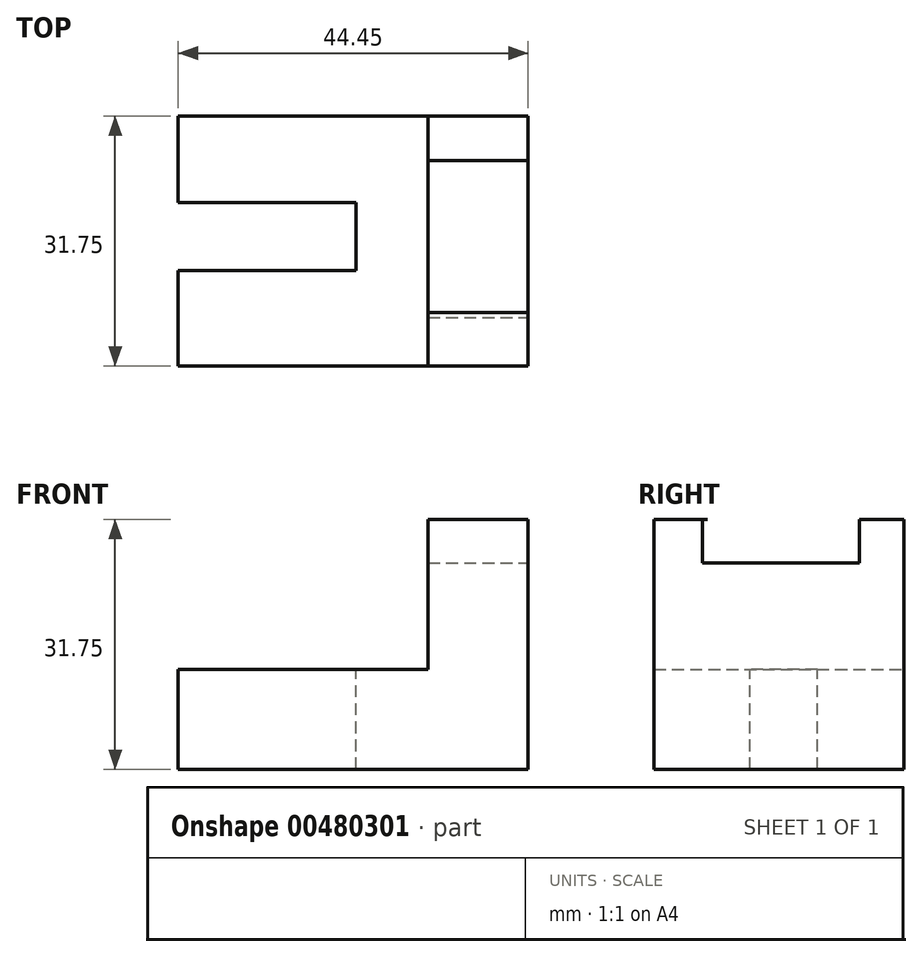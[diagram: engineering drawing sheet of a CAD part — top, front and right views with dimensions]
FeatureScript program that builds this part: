
annotation { "Feature Type Name" : "Feature", "Feature Type Description" : "" }
export const myFeature = defineFeature(function(context is Context, id is Id, definition is map)
    precondition{}
    {
        {
            var Q0;
            Q0=qCreatedBy(makeId("Front.planeOp"),FACE);
            var sketch = newSketch(context, id + "F0", { "sketchPlane" : qUnion([Q0])});
            skLineSegment(sketch, "E0", {"start": v(0, 0) * mm, "end": v(-44.45, 0) * mm});
            skLineSegment(sketch, "E1", {"start": v(-44.45, 0) * mm, "end": v(-44.45, 12.7) * mm});
            skLineSegment(sketch, "E2", {"start": v(-44.45, 12.7) * mm, "end": v(-12.7, 12.7) * mm});
            skLineSegment(sketch, "E3", {"start": v(-12.7, 12.7) * mm, "end": v(-12.7, 31.75) * mm});
            skLineSegment(sketch, "E4", {"start": v(-12.7, 31.75) * mm, "end": v(0, 31.75) * mm});
            skLineSegment(sketch, "E5", {"start": v(0, 31.75) * mm, "end": v(0, 0) * mm});
            skSolve(sketch);
        }
        {
            var Q0;
            Q0 = qSketchRegion(id + "F0", true);
            extrude(context, id + "F1", {"entities" : qUnion([Q0]), "depth" : 31.75 * mm, "offsetDistance" : 25.4 * mm});
        }
        {
            var Q0;
            Q0=makeQuery(id+"F1.opExtrude","SWEPT_FACE",FACE,{"disambiguationData":[OSD([sQuery(id+"F0.wireOp",EDGE,"E2")])]});
            var sketch = newSketch(context, id + "F2", { "sketchPlane" : qUnion([Q0])});
            skLineSegment(sketch, "E6.bottom", {"start": v(-44.45, -11.01) * mm, "end": v(-21.87, -11.01) * mm});
            skLineSegment(sketch, "E6.top", {"start": v(-44.45, -19.6) * mm, "end": v(-21.87, -19.6) * mm});
            skLineSegment(sketch, "E6.left", {"start": v(-44.45, -11.01) * mm, "end": v(-44.45, -19.6) * mm});
            skLineSegment(sketch, "E6.right", {"start": v(-21.87, -11.01) * mm, "end": v(-21.87, -19.6) * mm});
            skSolve(sketch);
        }
        {
            var Q0;
            Q0=makeQuery(id+"F2.imprint","IMPRINT",FACE,{"disambiguationData":[TD([[makeQuery(id+"F2.imprint","IMPRINT",EDGE,{"derivedFrom":sQuery(id+"F2.wireOp",EDGE,"E6.bottom")}),-1.0]])]});
            extrude(context, id + "F3", {"entities" : qUnion([Q0]), "operationType" : NewBodyOperationType.REMOVE, "oppositeDirection" : true, "depth" : 1320.8 * mm, "offsetDistance" : 25.4 * mm});
        }
        {
            var Q0;
            Q0=qCreatedBy(makeId("Right.planeOp"),FACE);
            var sketch = newSketch(context, id + "F4", { "sketchPlane" : qUnion([Q0])});
            skLineSegment(sketch, "E7", {"start": v(-25.6, 31.74) * mm, "end": v(-25.6, 26.24) * mm});
            skLineSegment(sketch, "E8", {"start": v(-25.6, 26.24) * mm, "end": v(-5.67, 26.24) * mm});
            skLineSegment(sketch, "E9", {"start": v(-5.67, 26.24) * mm, "end": v(-5.67, 31.9) * mm});
            skLineSegment(sketch, "E10", {"start": v(-5.67, 31.9) * mm, "end": v(-25.6, 31.74) * mm});
            skSolve(sketch);
        }
        {
            var Q0;
            Q0=makeQuery(id+"F4.imprint","IMPRINT",FACE,{"disambiguationData":[TD([[makeQuery(id+"F4.imprint","IMPRINT",EDGE,{"derivedFrom":sQuery(id+"F4.wireOp",EDGE,"E7")}),1.0]])]});
            extrude(context, id + "F5", {"entities" : qUnion([Q0]), "operationType" : NewBodyOperationType.REMOVE, "oppositeDirection" : true, "depth" : 127 * mm, "offsetDistance" : 25.4 * mm});
        }
    });
